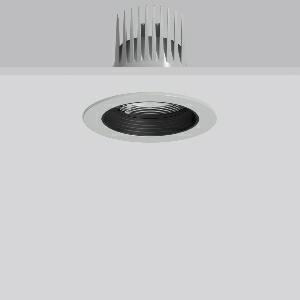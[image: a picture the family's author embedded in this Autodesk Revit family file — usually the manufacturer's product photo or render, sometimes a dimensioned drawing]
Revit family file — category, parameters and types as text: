
# Revit family: heledon_maxi_e_901762_004_1_3bb0
name_source: partatom
category: Lighting Fixtures
units: mm (PartAtom-declared; Revit-internal decimal feet)

## family parameters
Cut with Voids When Loaded = No
Host = Face
Light Source = No
Part Type = Normal
Room Calculation Point = No
Round Connector Dimension = Use Diameter
Shared = No

## types (1)
- HELEDON maxi E (1 x LED Modul 940, 2950 lm, 4000)
    Apparent Load = 25 VA
    Approval mark = CE
    CIE Flux Codes = 96 100 100 100 100
    Color Rendering = 92
    Color Temperature = 4000
    Default Elevation = 1800 mm
    Description = Series: HELEDON maxi
Round recessed downlight. Housing: die-cast aluminium, powder-coated. Black plastic ring and recessed LED to prevent glare from the side. Optical assembly with lens made of plastic (polycarbonate) for the best homogeneous light distribution - can be changed without tools. Best colour rendering index Ra>90. Suitable for Recessed ceiling mounting. Installation without tools thanks to spring fastening system. Including separate LED converter with connecting cable 600 mm.High quality converter without flickering and stroboscopic effect. Through-wiring box (5 pole) available as accessory. The following accessories can be mounted without use of tools: interchangeable lenses, decorative glasses, honeycomb louvre, clear and frosted diffusers, white interchangeable plastic ring. 
Colour: silver
Diameter: 162 mm
Height: 3 mm
Cut-out diameter: 152 mm
Recess height: 200 mm
Luminaire: recess height: 135 mm
Lamp: LED
Socket: without socket
Colour temperature: 4000K
Colour rendering index (CRI): 92
System power: 25 W
Rated luminous flux: 2950 lm
Luminous efficiency: 118 lm/W
Control gear: Regulated power supply
Protection class: II
Type of protection: IP 20
    Height = 0 mm  [stored 0 ft]
    Lamp = 1 x LED Modul 940
    Lamp Light Flux = 2950 lm
    Lamp count = 1
    Length = 162 mm
    Lifetime = 50000 h
    Luminous efficacy = 118 lm/W
    Manufacturer = RZB
    ModVariant = No
    Model = 901762.004.1
    Mounting Place = Ceiling
    Mounting Type = Recessed
    Number of Poles = 1
    OnlyDefault = Yes
    Power Factor = 1
    Product Name = HELEDON maxi E
    Product group = Recessed downlights
    ProductGroupID = 402
    Protection Class = Protection class II
    Protection Degree = IP 20
    RLX_Detail_Level = 1
    RLX_Emergency_Light_Flux = 0 lm
    RLX_Emergency_Type = 0
    RLX_Emergency_Type_DB = No
    RlxData = <blob elided: 119257 chars, md5=0d38f179>
    Socket = socket
    Standby Power = 0 W
    System Light Flux = 2950 lm
    System Power = 25 W
    Type Comments = Product without accessories
    Type Image = 901663.004.jpg
    URL = http://relux.com
    VarID = ---
    Voltage = 230 V
    Voltage Range = 220-240 V
    Weight = 0.00 kg
    Width = 0 mm  [stored 0 ft]

note: [stored X ft] marks values corroborated as IEEE doubles in the binary element streams (Revit-internal decimal feet)

## geometry (parser evidence)
native form markers: Blend x4, Sweep x11
no freeform markers — native parametric forms only
